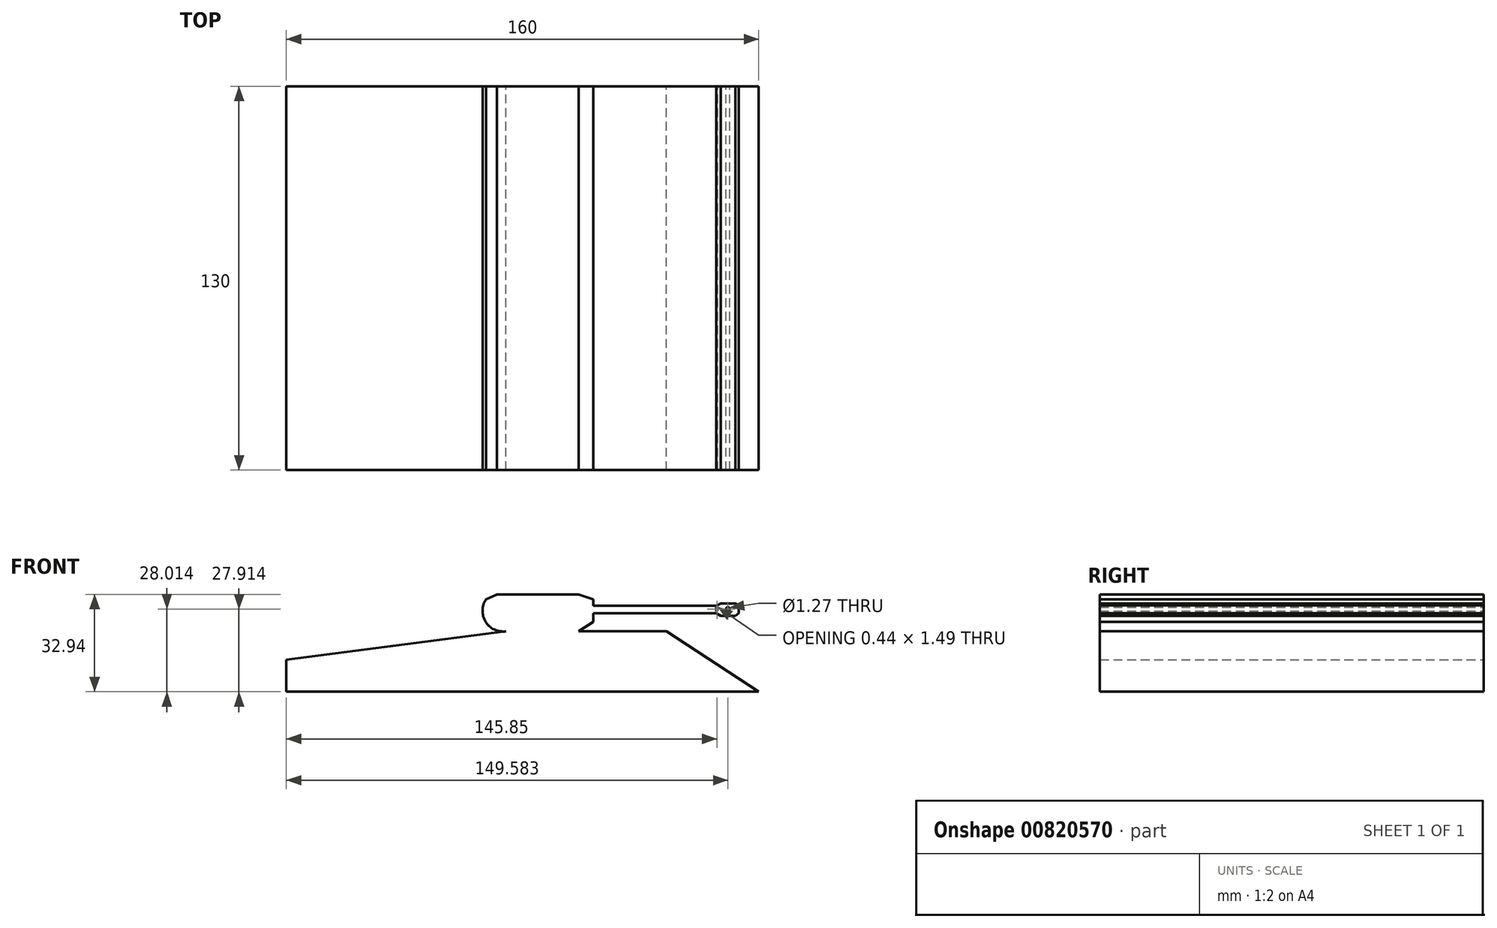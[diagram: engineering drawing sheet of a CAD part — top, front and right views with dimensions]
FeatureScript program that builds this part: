
annotation { "Feature Type Name" : "Feature", "Feature Type Description" : "" }
export const myFeature = defineFeature(function(context is Context, id is Id, definition is map)
    precondition{}
    {
        {
            var Q0;
            Q0=qCreatedBy(makeId("Front.planeOp"),FACE);
            var sketch = newSketch(context, id + "F0", { "sketchPlane" : qUnion([Q0])});
            skLineSegment(sketch, "E0", {"start": v(-86.65, 20.9) * mm, "end": v(-86.65, 10.13) * mm});
            skLineSegment(sketch, "E1", {"start": v(-12.3, 30.56) * mm, "end": v(-86.65, 20.9) * mm});
            skPoint(sketch, "E2.start.orphan", {"position": v(-10.82, 30.56) * mm});
            skLineSegment(sketch, "E3", {"start": v(-12.3, 30.56) * mm, "end": v(42.02, 30.56) * mm});
            skLineSegment(sketch, "E4", {"start": v(42.02, 30.56) * mm, "end": v(73.35, 10.13) * mm});
            skPoint(sketch, "E5.orphan", {"position": v(-86.65, 30.56) * mm});
            skArc(sketch, "E6", {"start": v(-19.01, 41.42) * mm, "mid": v(-19.17, 33.83) * mm, "end": v(-12.3, 30.56) * mm});
            skLineSegment(sketch, "E7", {"start": v(-19.01, 41.42) * mm, "end": v(-15.35, 43.07) * mm});
            skLineSegment(sketch, "E8", {"start": v(-15.35, 43.07) * mm, "end": v(12.4, 43.07) * mm});
            skLineSegment(sketch, "E9", {"start": v(12.4, 43.07) * mm, "end": v(17.34, 41.42) * mm});
            skLineSegment(sketch, "E10", {"start": v(17.34, 41.42) * mm, "end": v(17.34, 33.73) * mm});
            skLineSegment(sketch, "E11", {"start": v(17.34, 33.73) * mm, "end": v(12.4, 30.56) * mm});
            skLineSegment(sketch, "E12", {"start": v(73.35, 10.13) * mm, "end": v(-86.65, 10.13) * mm});
            skPoint(sketch, "E13.orphan", {"position": v(-86.65, -17.44) * mm});
            skLineSegment(sketch, "E14", {"start": v(17.34, 39.28) * mm, "end": v(58.98, 39.28) * mm});
            skLineSegment(sketch, "E15", {"start": v(58.98, 39.28) * mm, "end": v(58.98, 36.7) * mm});
            skLineSegment(sketch, "E16", {"start": v(58.98, 36.7) * mm, "end": v(17.34, 36.7) * mm});
            skLineSegment(sketch, "E17", {"start": v(58.98, 39.28) * mm, "end": v(60.44, 40.06) * mm});
            skLineSegment(sketch, "E18", {"start": v(58.98, 36.7) * mm, "end": v(60.44, 35.8) * mm});
            skLineSegment(sketch, "E19", {"start": v(60.44, 35.8) * mm, "end": v(65.39, 35.8) * mm});
            skLineSegment(sketch, "E20", {"start": v(65.39, 35.8) * mm, "end": v(66.63, 36.7) * mm});
            skLineSegment(sketch, "E21", {"start": v(66.63, 36.7) * mm, "end": v(66.63, 39.34) * mm});
            skLineSegment(sketch, "E22", {"start": v(66.63, 39.34) * mm, "end": v(65.39, 40.06) * mm});
            skLineSegment(sketch, "E23", {"start": v(65.39, 40.06) * mm, "end": v(60.44, 40.06) * mm});
            skCircle(sketch, "E24", {"center": v(62.93, 38.14) * mm, "radius": 0.64 * mm});
            skArc(sketch, "E25", {"start": v(58.98, 37.3) * mm, "mid": v(59.42, 38.04) * mm, "end": v(58.98, 38.79) * mm});
            skSolve(sketch);
        }
        {
            var Q0;
            Q0 = qSketchRegion(id + "F0", true);
            extrude(context, id + "F1", {"entities" : qUnion([Q0]), "depth" : 130 * mm, "offsetDistance" : 25 * mm});
        }
    });
